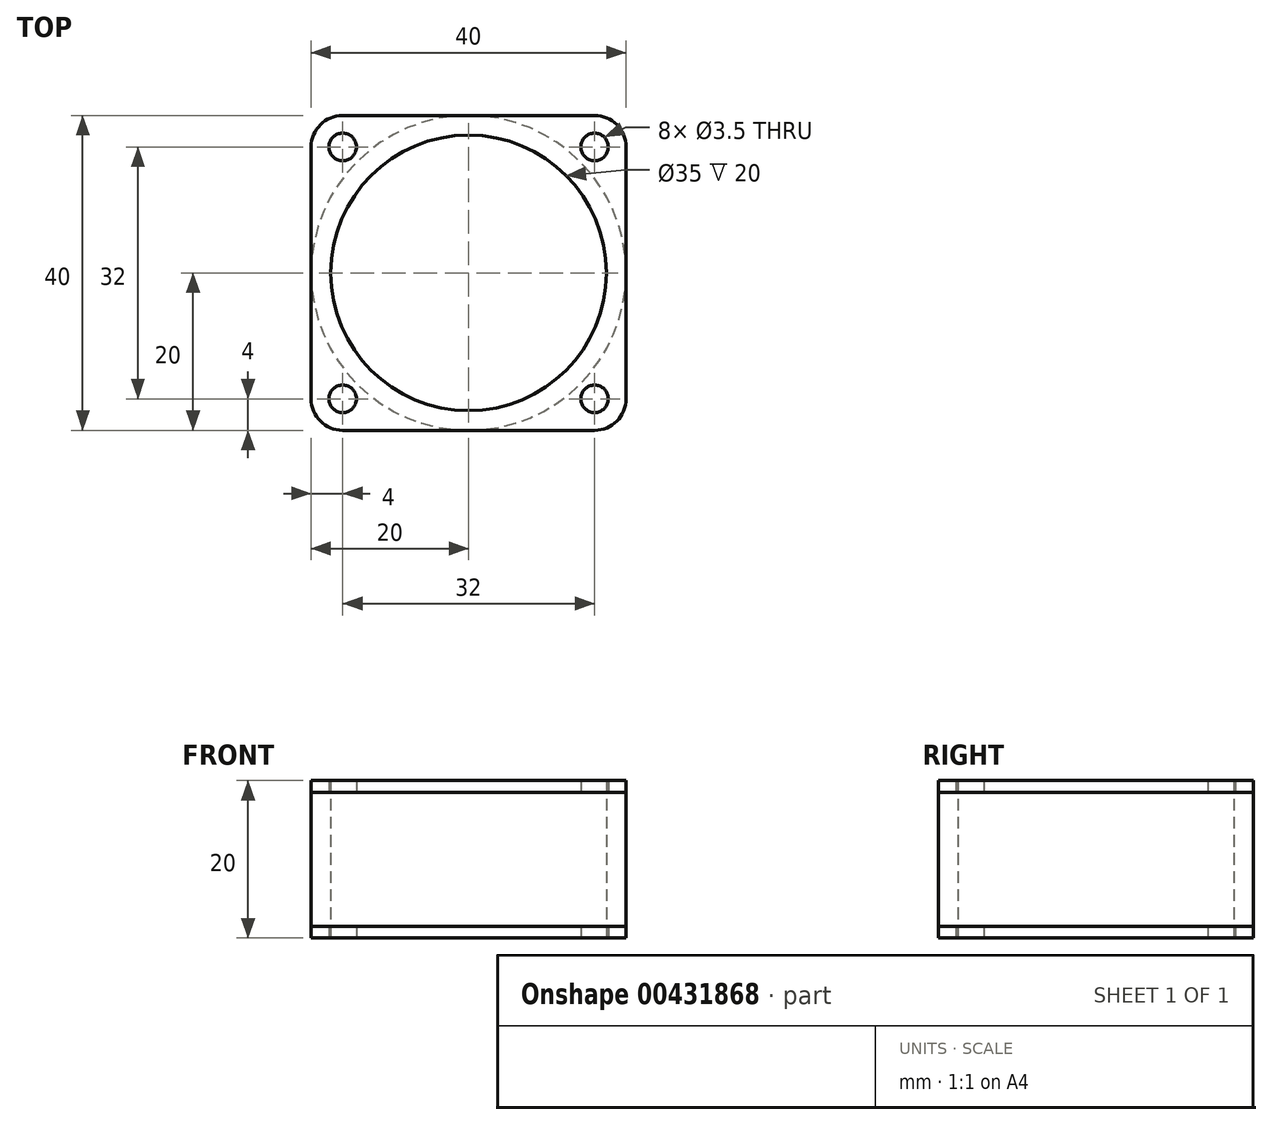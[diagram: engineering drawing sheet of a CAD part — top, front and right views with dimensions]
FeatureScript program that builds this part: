
annotation { "Feature Type Name" : "Feature", "Feature Type Description" : "" }
export const myFeature = defineFeature(function(context is Context, id is Id, definition is map)
    precondition{}
    {
        {
            var Q0;
            Q0=qCreatedBy(makeId("Front.planeOp"),FACE);
            var sketch = newSketch(context, id + "F0", { "sketchPlane" : qUnion([Q0])});
            skLineSegment(sketch, "E0.bottom", {"start": v(-20, 10) * mm, "end": v(20, 10) * mm});
            skLineSegment(sketch, "E0.top", {"start": v(-20, -10) * mm, "end": v(20, -10) * mm});
            skLineSegment(sketch, "E0.left", {"start": v(-20, 10) * mm, "end": v(-20, -10) * mm});
            skLineSegment(sketch, "E0.right", {"start": v(20, 10) * mm, "end": v(20, -10) * mm});
            skLineSegment(sketch, "E1.bottom", {"start": v(-42.98, 8.5) * mm, "end": v(-18.5, 8.5) * mm});
            skLineSegment(sketch, "E1.top", {"start": v(-42.98, -8.5) * mm, "end": v(-18.5, -8.5) * mm});
            skLineSegment(sketch, "E1.left", {"start": v(-42.98, 8.5) * mm, "end": v(-42.98, -8.5) * mm});
            skLineSegment(sketch, "E1.right", {"start": v(-18.5, 8.5) * mm, "end": v(-18.5, -8.5) * mm});
            skLineSegment(sketch, "E2", {"start": v(0, 0) * mm, "end": v(0, 18.8) * mm});
            skSolve(sketch);
        }
        {
            var Q0;
            {var subQ5=sQuery(id+"F0.wireOp",EDGE,"E1.right");Q0=makeQuery(id+"F0.imprint","IMPRINT",FACE,{"disambiguationData":[TD([[makeQuery(id+"F0.imprint","IMPRINT",EDGE,{"derivedFrom":subQ5}),-1.0]])]});}
            var Q1;
            {var subQ4=sQuery(id+"F0.wireOp",EDGE,"E0.bottom");Q1=makeQuery(id+"F0.imprint","IMPRINT",FACE,{"disambiguationData":[TD([[makeQuery(id+"F0.imprint","IMPRINT",EDGE,{"derivedFrom":subQ4}),-1.0]])]});}
            extrude(context, id + "F1", {"entities" : qUnion([Q0, Q1]), "endBound" : BoundingType.SYMMETRIC, "depth" : 40 * mm});
        }
        {
            var Q0;
            Q0=makeQuery(id+"F1.opExtrude","CAP_EDGE",EDGE,{"disambiguationData":[OSD([sQuery(id+"F0.wireOp",EDGE,"E0.left")])],"isStart":false});
            var Q1;
            Q1=makeQuery(id+"F1.opExtrude","CAP_EDGE",EDGE,{"disambiguationData":[OSD([sQuery(id+"F0.wireOp",EDGE,"E0.right")])],"isStart":false});
            var Q2;
            Q2=makeQuery(id+"F1.opExtrude","CAP_EDGE",EDGE,{"disambiguationData":[OSD([sQuery(id+"F0.wireOp",EDGE,"E0.right")])],"isStart":true});
            var Q3;
            Q3=makeQuery(id+"F1.opExtrude","CAP_EDGE",EDGE,{"disambiguationData":[OSD([sQuery(id+"F0.wireOp",EDGE,"E0.left")])],"isStart":true});
            fillet(context, id + "F2", {"entities" : qUnion([Q0, Q1, Q2, Q3]), "radius" : 4 * mm, "tangentPropagation" : true, "allowEdgeOverflow" : false});
        }
        {
            var Q0;
            Q0=makeQuery(id+"F1.opExtrude","SWEPT_FACE",FACE,{"disambiguationData":[OSD([sQuery(id+"F0.wireOp",EDGE,"E0.top")])]});
            var sketch = newSketch(context, id + "F3", { "sketchPlane" : qUnion([Q0])});
            skPoint(sketch, "E3", {"position": v(-16, 16) * mm});
            skPoint(sketch, "E4", {"position": v(16, 16) * mm});
            skPoint(sketch, "E5", {"position": v(16, -16) * mm});
            skPoint(sketch, "E6", {"position": v(-16, -16) * mm});
            skPoint(sketch, "E7.0", {"position": v(0, 0) * mm});
            skSolve(sketch);
        }
        {
            var Q0;
            Q0=sQuery(id+"F3.wireOp",VERTEX,"E3");
            var Q1;
            Q1=sQuery(id+"F3.wireOp",VERTEX,"E4");
            var Q2;
            Q2=sQuery(id+"F3.wireOp",VERTEX,"E5");
            var Q3;
            Q3=sQuery(id+"F3.wireOp",VERTEX,"E6");
            var Q4;
            Q4=makeQuery(id+"F1.opExtrude","SWEPT_BODY",BODY,{"disambiguationData":[OSD([sQuery(id+"F0.wireOp",EDGE,"E0.bottom"),sQuery(id+"F0.wireOp",EDGE,"E0.top"),sQuery(id+"F0.wireOp",EDGE,"E0.left"),sQuery(id+"F0.wireOp",EDGE,"E0.right")])]});
            hole(context, id + "F4", {"style" : HoleStyle.SIMPLE, "endStyle" : HoleEndStyle.THROUGH, "holeDiameter" : 3.5 * mm, "isTappedThrough" : true, "tappedDepth" : 12 * mm, "tapClearance" : 3, "locations" : qUnion([Q0, Q1, Q2, Q3]), "scope" : qUnion([Q4])});
        }
        {
            var Q0;
            {var subQ5=sQuery(id+"F0.wireOp",EDGE,"E1.left");Q0=makeQuery(id+"F0.imprint","IMPRINT",FACE,{"disambiguationData":[TD([[makeQuery(id+"F0.imprint","IMPRINT",EDGE,{"derivedFrom":subQ5}),1.0]])]});}
            var Q1;
            Q1=sQuery(id+"F0.wireOp",EDGE,"E2");
            revolve(context, id + "F5", {"operationType" : NewBodyOperationType.REMOVE, "entities" : qUnion([Q0]), "axis" : qUnion([Q1]), "revolveType" : RevolveType.FULL, "oppositeDirection" : true});
        }
        {
            var Q0;
            Q0=sQuery(id+"F3.wireOp",VERTEX,"E7.0");
            var Q1;
            Q1=makeQuery(id+"F1.opExtrude","SWEPT_BODY",BODY,{"disambiguationData":[OSD([sQuery(id+"F0.wireOp",EDGE,"E0.bottom"),sQuery(id+"F0.wireOp",EDGE,"E0.top"),sQuery(id+"F0.wireOp",EDGE,"E0.left"),sQuery(id+"F0.wireOp",EDGE,"E0.right")])]});
            hole(context, id + "F6", {"style" : HoleStyle.SIMPLE, "endStyle" : HoleEndStyle.THROUGH, "holeDiameter" : 35 * mm, "isTappedThrough" : true, "tappedDepth" : 12 * mm, "tapClearance" : 3, "locations" : qUnion([Q0]), "scope" : qUnion([Q1])});
        }
    });
